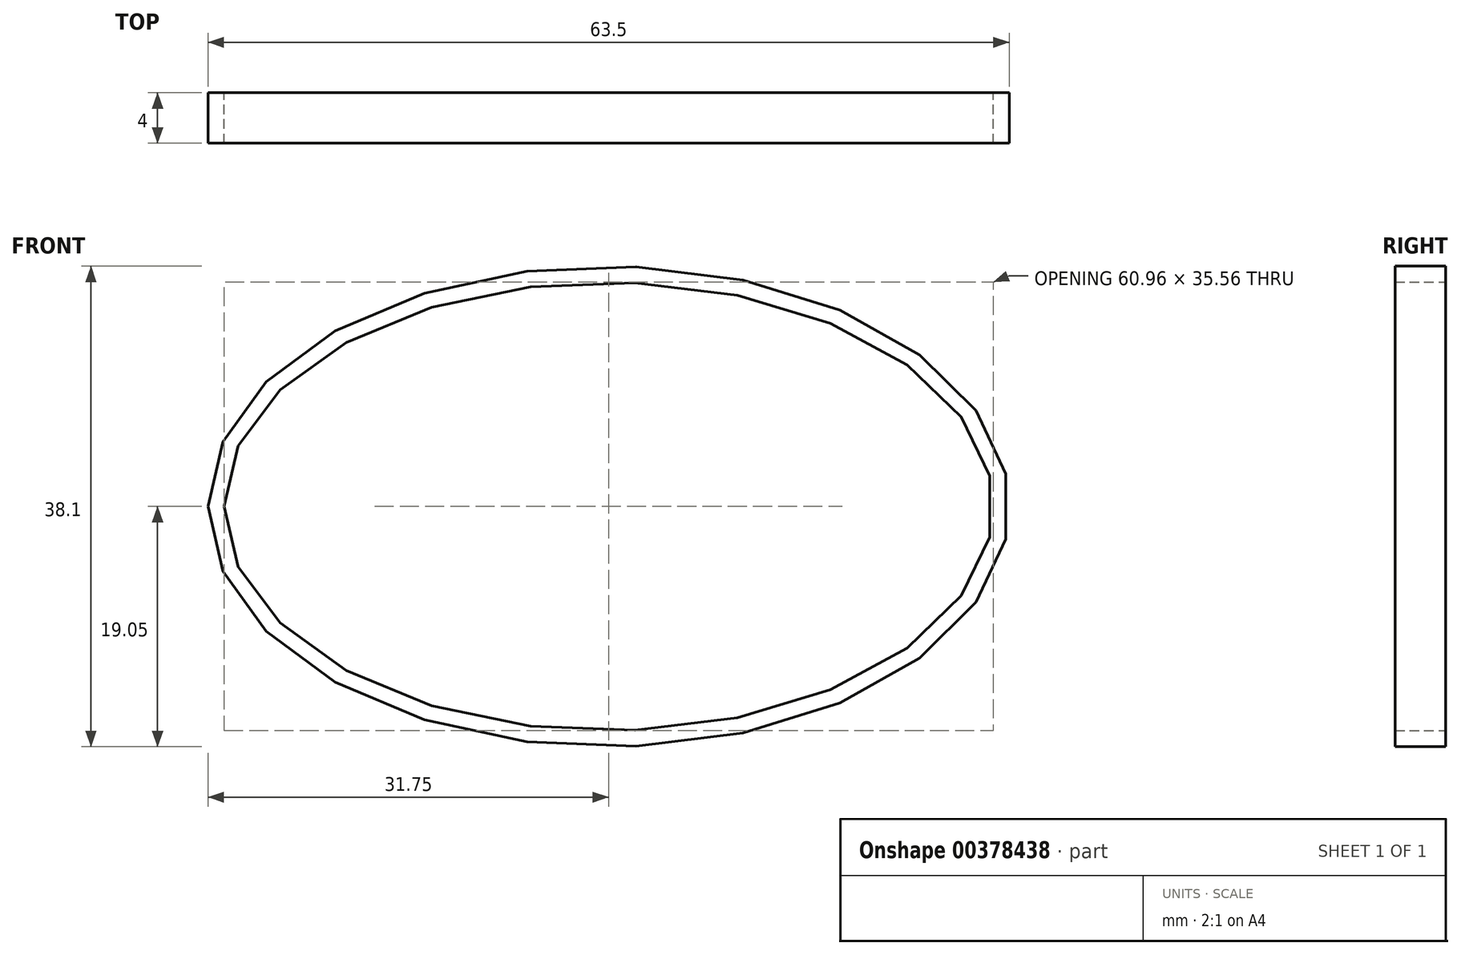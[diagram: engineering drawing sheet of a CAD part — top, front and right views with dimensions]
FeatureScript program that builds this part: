
annotation { "Feature Type Name" : "Feature", "Feature Type Description" : "" }
export const myFeature = defineFeature(function(context is Context, id is Id, definition is map)
    precondition{}
    {
        {
            var Q0;
            Q0=qCreatedBy(makeId("Front.planeOp"),FACE);
            var sketch = newSketch(context, id + "F0", { "sketchPlane" : qUnion([Q0])});
            skEllipse(sketch, "E0", {"center": v(0, 0) * mm, "majorRadius": 31.75 * mm, "minorRadius": 19.05 * mm, "majorAxis": v(-1, 0)});
            skEllipse(sketch, "E1", {"center": v(0, 0) * mm, "majorRadius": 30.48 * mm, "minorRadius": 17.78 * mm, "majorAxis": v(-1, 0)});
            skSolve(sketch);
        }
        {
            var Q0;
            Q0=makeQuery(id+"F0.imprint","IMPRINT",FACE,{"disambiguationData":[TD([[makeQuery(id+"F0.imprint","IMPRINT",EDGE,{"derivedFrom":sQuery(id+"F0.wireOp",EDGE,"E0")}),1.0]])]});
            var Q1;
            Q1=sQuery(id+"F0.wireOp",EDGE,"E0");
            extrude(context, id + "F1", {"entities" : qUnion([Q0]), "surfaceEntities" : qUnion([Q1]), "depth" : 4 * mm});
        }
    });
